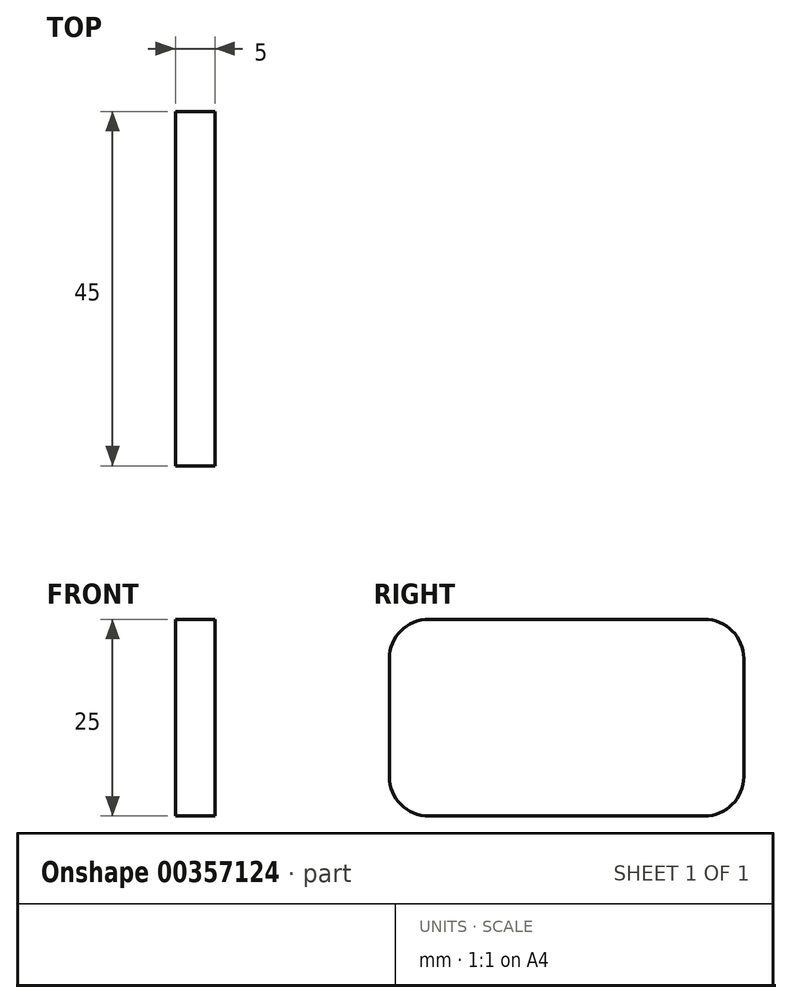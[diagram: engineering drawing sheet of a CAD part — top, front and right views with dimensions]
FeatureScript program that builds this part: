
annotation { "Feature Type Name" : "Feature", "Feature Type Description" : "" }
export const myFeature = defineFeature(function(context is Context, id is Id, definition is map)
    precondition{}
    {
        {
            var Q0;
            Q0=qCreatedBy(makeId("Right.planeOp"),FACE);
            var sketch = newSketch(context, id + "F0", { "sketchPlane" : qUnion([Q0])});
            skLineSegment(sketch, "E0.bottom", {"start": v(-22.5, -12.5) * mm, "end": v(22.5, -12.5) * mm});
            skLineSegment(sketch, "E0.top", {"start": v(-22.5, 12.5) * mm, "end": v(22.5, 12.5) * mm});
            skLineSegment(sketch, "E0.left", {"start": v(-22.5, -12.5) * mm, "end": v(-22.5, 12.5) * mm});
            skLineSegment(sketch, "E0.right", {"start": v(22.5, -12.5) * mm, "end": v(22.5, 12.5) * mm});
            skPoint(sketch, "E0.middle", {"position": v(0, 0) * mm});
            skSolve(sketch);
        }
        {
            var Q0;
            Q0 = qSketchRegion(id + "F0", true);
            extrude(context, id + "F1", {"entities" : qUnion([Q0]), "depth" : 5 * mm});
        }
        {
            var Q0;
            Q0=makeQuery(id+"F1.opExtrude","SWEPT_EDGE",EDGE,{"disambiguationData":[OSD([sQuery(id+"F0.wireOp",EDGE,"E0.bottom"),sQuery(id+"F0.wireOp",EDGE,"E0.left")])]});
            var Q1;
            Q1=makeQuery(id+"F1.opExtrude","SWEPT_EDGE",EDGE,{"disambiguationData":[OSD([sQuery(id+"F0.wireOp",EDGE,"E0.top"),sQuery(id+"F0.wireOp",EDGE,"E0.left")])]});
            var Q2;
            Q2=makeQuery(id+"F1.opExtrude","SWEPT_EDGE",EDGE,{"disambiguationData":[OSD([sQuery(id+"F0.wireOp",EDGE,"E0.top"),sQuery(id+"F0.wireOp",EDGE,"E0.right")])]});
            var Q3;
            Q3=makeQuery(id+"F1.opExtrude","SWEPT_EDGE",EDGE,{"disambiguationData":[OSD([sQuery(id+"F0.wireOp",EDGE,"E0.bottom"),sQuery(id+"F0.wireOp",EDGE,"E0.right")])]});
            fillet(context, id + "F2", {"entities" : qUnion([Q0, Q1, Q2, Q3]), "radius" : 5 * mm, "tangentPropagation" : true, "allowEdgeOverflow" : false});
        }
    });
